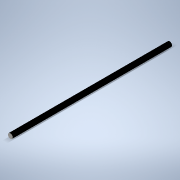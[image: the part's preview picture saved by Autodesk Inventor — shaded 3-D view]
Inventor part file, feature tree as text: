
AUTODESK INVENTOR PART (.ipt)
format: ipt  version: 2020 (Build 240168000, 168)  size: 95,744 bytes
history: native  units: in
note: dims shown in document units (in); Inventor stores cm internally (conversion verified against a paired STEP export)
features: extrude x1, sketch x1
ambient origin geometry x8: Origin, YZ Plane, XZ Plane, XY Plane, X Axis, Y Axis, Z Axis, Center Point
bodies: Solid1 (feature_tree)
feature tree (2):
  extrude  "Extrusion1"  Depth=39.3701in TaperAngle=0.0deg
  sketch  "Sketch1"  dims[d0=1.1811in d1=39.3701in d2=0.0in]
